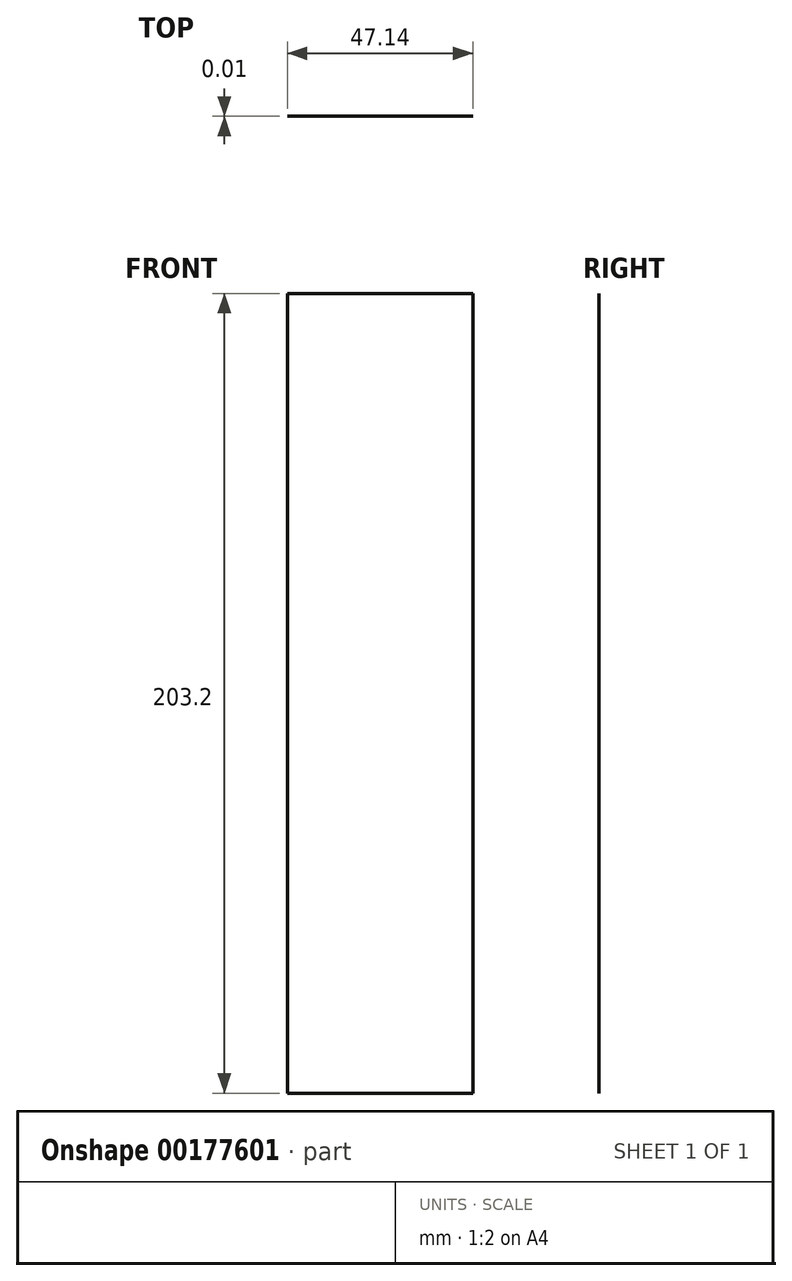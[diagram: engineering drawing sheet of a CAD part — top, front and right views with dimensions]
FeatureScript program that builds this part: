
annotation { "Feature Type Name" : "Feature", "Feature Type Description" : "" }
export const myFeature = defineFeature(function(context is Context, id is Id, definition is map)
    precondition{}
    {
        {
            var Q0;
            Q0=qCreatedBy(makeId("Front.planeOp"),FACE);
            var sketch = newSketch(context, id + "F0", { "sketchPlane" : qUnion([Q0])});
            skLineSegment(sketch, "E0.bottom", {"start": v(-27.16, 143.75) * mm, "end": v(23.64, 143.75) * mm});
            skLineSegment(sketch, "E0.top", {"start": v(-27.16, -59.45) * mm, "end": v(23.64, -59.45) * mm});
            skLineSegment(sketch, "E0.left", {"start": v(-27.16, 143.75) * mm, "end": v(-27.16, -59.45) * mm});
            skLineSegment(sketch, "E0.right", {"start": v(23.64, 143.75) * mm, "end": v(23.64, -59.45) * mm});
            skSolve(sketch);
        }
        {
            var Q0;
            Q0 = qSketchRegion(id + "F0", true);
            extrude(context, id + "F1", {"entities" : qUnion([Q0]), "depth" : 3 / 203.2 * mm});
        }
        {
            var Q0;
            Q0=makeQuery(id+"F1.opExtrude","CAP_EDGE",EDGE,{"disambiguationData":[OSD([sQuery(id+"F0.wireOp",EDGE,"E0.right")])],"isStart":false});
            chamfer(context, id + "F2", {"entities" : qUnion([Q0]), "chamferType" : ChamferType.OFFSET_ANGLE, "width" : 6.35 * mm, "oppositeDirection" : false, "angle" : 30 * degree, "tangentPropagation" : true});
        }
    });
